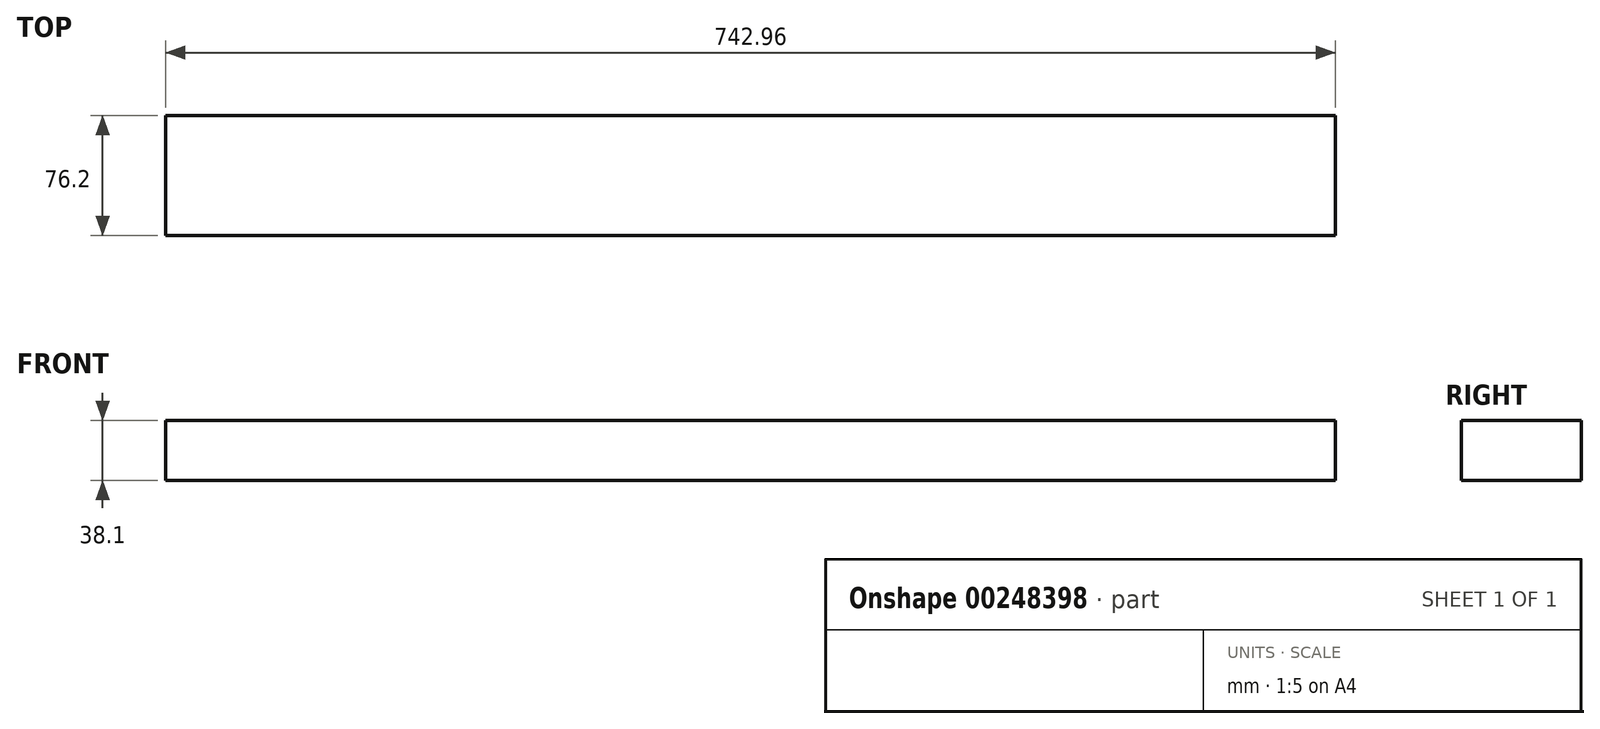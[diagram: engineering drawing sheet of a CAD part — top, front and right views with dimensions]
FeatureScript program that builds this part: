
annotation { "Feature Type Name" : "Feature", "Feature Type Description" : "" }
export const myFeature = defineFeature(function(context is Context, id is Id, definition is map)
    precondition{}
    {
        {
            var Q0;
            Q0=qCreatedBy(makeId("Right.planeOp"),FACE);
            var sketch = newSketch(context, id + "F0", { "sketchPlane" : qUnion([Q0])});
            skLineSegment(sketch, "E0.bottom", {"start": v(38.1, 19.05) * mm, "end": v(-38.1, 19.05) * mm});
            skLineSegment(sketch, "E0.top", {"start": v(38.1, -19.05) * mm, "end": v(-38.1, -19.05) * mm});
            skLineSegment(sketch, "E0.left", {"start": v(38.1, 19.05) * mm, "end": v(38.1, -19.05) * mm});
            skLineSegment(sketch, "E0.right", {"start": v(-38.1, 19.05) * mm, "end": v(-38.1, -19.05) * mm});
            skPoint(sketch, "E0.middle", {"position": v(0, 0) * mm});
            skSolve(sketch);
        }
        {
            var Q0;
            Q0=makeQuery(id+"F0.imprint","IMPRINT",FACE,{"disambiguationData":[TD([[makeQuery(id+"F0.imprint","IMPRINT",EDGE,{"derivedFrom":sQuery(id+"F0.wireOp",EDGE,"E0.bottom")}),1.0]])]});
            extrude(context, id + "F1", {"entities" : qUnion([Q0]), "endBound" : BoundingType.SYMMETRIC, "depth" : 742.95 * mm});
        }
    });
